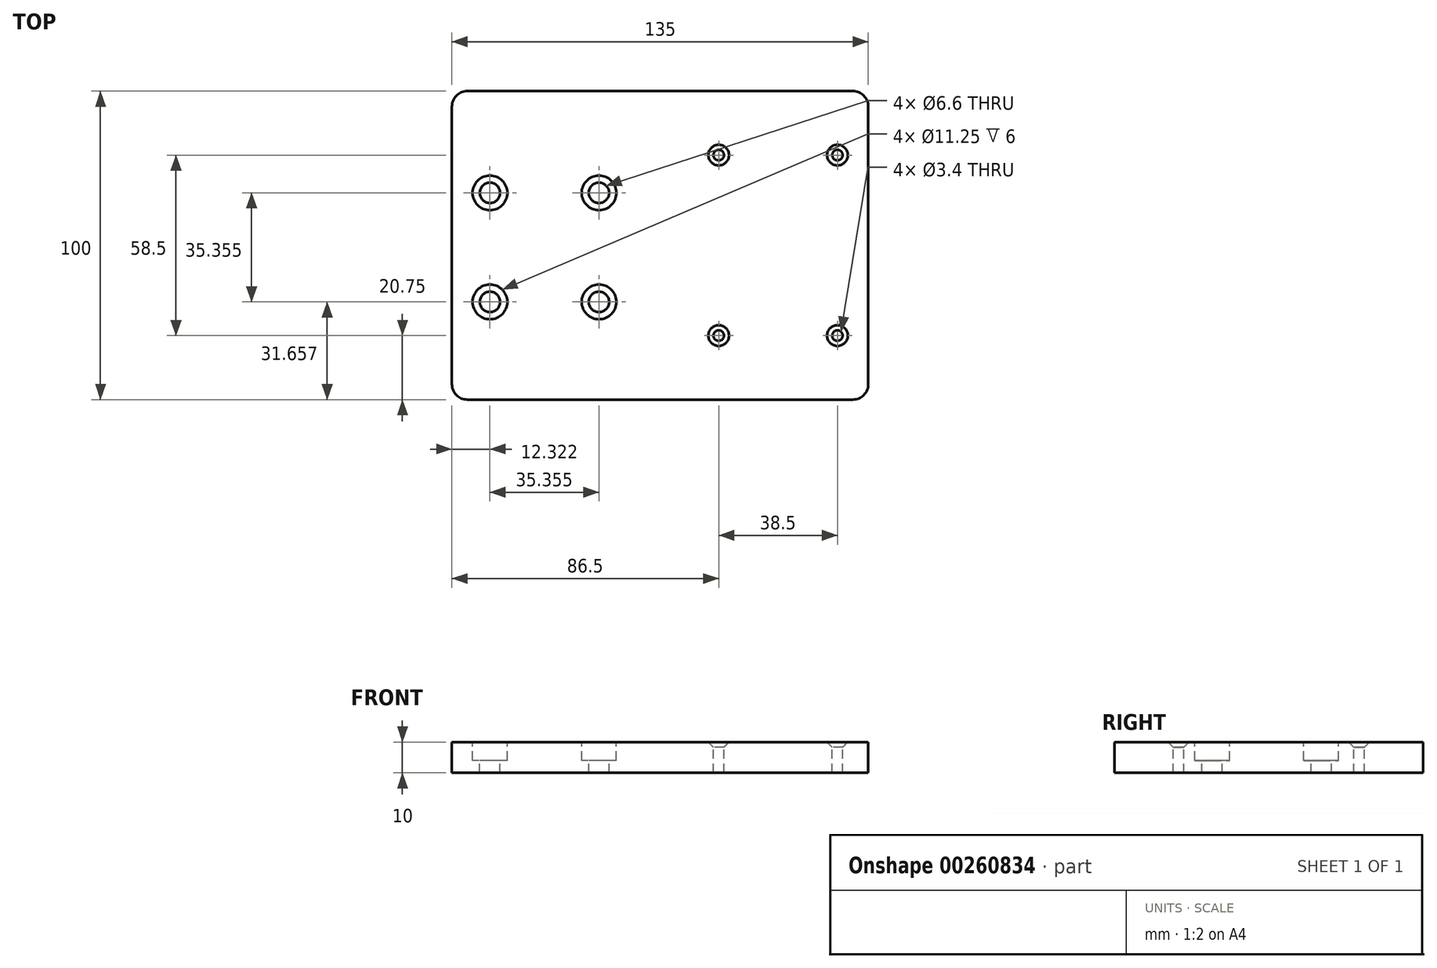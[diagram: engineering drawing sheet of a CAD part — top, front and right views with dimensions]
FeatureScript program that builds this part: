
annotation { "Feature Type Name" : "Feature", "Feature Type Description" : "" }
export const myFeature = defineFeature(function(context is Context, id is Id, definition is map)
    precondition{}
    {
        {
            var Q0;
            Q0=qCreatedBy(makeId("Top.planeOp"),FACE);
            var sketch = newSketch(context, id + "F0", { "sketchPlane" : qUnion([Q0])});
            skLineSegment(sketch, "E0.bottom", {"start": v(0, 0) * mm, "end": v(135, 0) * mm});
            skLineSegment(sketch, "E0.top", {"start": v(0, 100) * mm, "end": v(135, 100) * mm});
            skLineSegment(sketch, "E0.left", {"start": v(0, 0) * mm, "end": v(0, 100) * mm});
            skLineSegment(sketch, "E0.right", {"start": v(135, 0) * mm, "end": v(135, 100) * mm});
            skSolve(sketch);
        }
        {
            var Q0;
            Q0 = qSketchRegion(id + "F0", true);
            extrude(context, id + "F1", {"entities" : qUnion([Q0]), "offsetDistance" : 25 * mm, "depth" : 10 * mm});
        }
        {
            var Q0;
            Q0=makeQuery(id+"F1.opExtrude","CAP_FACE",FACE,{"disambiguationData":[OSD([sQuery(id+"F0.wireOp",EDGE,"E0.bottom"),sQuery(id+"F0.wireOp",EDGE,"E0.top"),sQuery(id+"F0.wireOp",EDGE,"E0.left"),sQuery(id+"F0.wireOp",EDGE,"E0.right")])],"isStart":false});
            var sketch = newSketch(context, id + "F2", { "sketchPlane" : qUnion([Q0])});
            skPoint(sketch, "E1", {"position": v(110, 90) * mm});
            skPoint(sketch, "E2", {"position": v(110, 10) * mm});
            skSolve(sketch);
        }
        {
            var Q0;
            Q0=makeQuery(id+"F1.opExtrude","CAP_FACE",FACE,{"disambiguationData":[OSD([sQuery(id+"F0.wireOp",EDGE,"E0.bottom"),sQuery(id+"F0.wireOp",EDGE,"E0.top"),sQuery(id+"F0.wireOp",EDGE,"E0.left"),sQuery(id+"F0.wireOp",EDGE,"E0.right")])],"isStart":false});
            var sketch = newSketch(context, id + "F3", { "sketchPlane" : qUnion([Q0])});
            skCircle(sketch, "E3", {"center": v(30, 49.33) * mm, "radius": 25 * mm, "construction": true});
            skLineSegment(sketch, "E4", {"start": v(30, 49.33) * mm, "end": v(5, 49.33) * mm, "construction": true});
            skLineSegment(sketch, "E5", {"start": v(30, 49.33) * mm, "end": v(12.32, 67.01) * mm, "construction": true});
            skLineSegment(sketch, "E6", {"start": v(30, 49.33) * mm, "end": v(47.68, 31.66) * mm, "construction": true});
            skLineSegment(sketch, "E7.bottom", {"start": v(12.32, 67.01) * mm, "end": v(47.68, 67.01) * mm, "construction": true});
            skLineSegment(sketch, "E7.top", {"start": v(12.32, 31.66) * mm, "end": v(47.68, 31.66) * mm, "construction": true});
            skLineSegment(sketch, "E7.left", {"start": v(12.32, 67.01) * mm, "end": v(12.32, 31.66) * mm, "construction": true});
            skLineSegment(sketch, "E7.right", {"start": v(47.68, 67.01) * mm, "end": v(47.68, 31.66) * mm, "construction": true});
            skPoint(sketch, "E8", {"position": v(12.32, 67.01) * mm});
            skPoint(sketch, "E9", {"position": v(47.68, 67.01) * mm});
            skPoint(sketch, "E10", {"position": v(47.68, 31.66) * mm});
            skPoint(sketch, "E11", {"position": v(12.32, 31.66) * mm});
            skSolve(sketch);
        }
        {
            var Q0;
            Q0=sQuery(id+"F3.wireOp",VERTEX,"E8");
            var Q1;
            Q1=sQuery(id+"F3.wireOp",VERTEX,"E9");
            var Q2;
            Q2=sQuery(id+"F3.wireOp",VERTEX,"E10");
            var Q3;
            Q3=sQuery(id+"F3.wireOp",VERTEX,"E11");
            var Q4;
            Q4=makeQuery(id+"F1.opExtrude","SWEPT_BODY",BODY,{"disambiguationData":[OSD([sQuery(id+"F0.wireOp",EDGE,"E0.bottom"),sQuery(id+"F0.wireOp",EDGE,"E0.top"),sQuery(id+"F0.wireOp",EDGE,"E0.left"),sQuery(id+"F0.wireOp",EDGE,"E0.right")])]});
            hole(context, id + "F4", {"style" : HoleStyle.C_BORE, "endStyle" : HoleEndStyle.THROUGH, "standardTappedOrClearance" : lookupTablePath({ "fit" : "Normal", "standard" : "ISO", "size" : "M6", "type" : "Clearance" }), "standardBlindInLast" : lookupTablePath({ "fit" : "Normal", "standard" : "ISO", "engagement" : "75%", "pitch" : "1 mm", "size" : "M6", "type" : "Clearance & tapped" }), "holeDiameter" : 6.6 * mm, "cBoreDiameter" : 11.25 * mm, "cBoreDepth" : 6 * mm, "majorDiameter" : 5 * mm, "tappedDepth" : 12 * mm, "tapClearance" : 3, "startFromSketch" : true, "locations" : qUnion([Q0, Q1, Q2, Q3]), "scope" : qUnion([Q4])});
        }
        {
            var Q0;
            Q0=makeQuery(id+"F1.opExtrude","SWEPT_EDGE",EDGE,{"disambiguationData":[OSD([sQuery(id+"F0.wireOp",EDGE,"E0.top"),sQuery(id+"F0.wireOp",EDGE,"E0.left")])]});
            var Q1;
            Q1=makeQuery(id+"F1.opExtrude","SWEPT_EDGE",EDGE,{"disambiguationData":[OSD([sQuery(id+"F0.wireOp",EDGE,"E0.top"),sQuery(id+"F0.wireOp",EDGE,"E0.right")])]});
            var Q2;
            Q2=makeQuery(id+"F1.opExtrude","SWEPT_EDGE",EDGE,{"disambiguationData":[OSD([sQuery(id+"F0.wireOp",EDGE,"E0.bottom"),sQuery(id+"F0.wireOp",EDGE,"E0.right")])]});
            var Q3;
            Q3=makeQuery(id+"F1.opExtrude","SWEPT_EDGE",EDGE,{"disambiguationData":[OSD([sQuery(id+"F0.wireOp",EDGE,"E0.bottom"),sQuery(id+"F0.wireOp",EDGE,"E0.left")])]});
            fillet(context, id + "F5", {"entities" : qUnion([Q0, Q1, Q2, Q3]), "radius" : 5 * mm, "tangentPropagation" : true, "allowEdgeOverflow" : false});
        }
        {
            var Q0;
            Q0=makeQuery(id+"F2.imprint","IMPRINT",FACE,{"disambiguationData":[TD([[makeQuery(id+"F2.imprint","IMPRINT",EDGE,{"derivedFrom":makeQuery(id+"F1.opExtrude","CAP_EDGE",EDGE,{"disambiguationData":[OSD([sQuery(id+"F0.wireOp",EDGE,"E0.bottom")])],"isStart":false})}),1.0]])]});
            var sketch = newSketch(context, id + "F6", { "sketchPlane" : qUnion([Q0])});
            skLineSegment(sketch, "E12.bottom", {"start": v(86.5, 20.75) * mm, "end": v(125, 20.75) * mm});
            skLineSegment(sketch, "E12.top", {"start": v(86.5, 79.25) * mm, "end": v(125, 79.25) * mm});
            skLineSegment(sketch, "E12.left", {"start": v(86.5, 20.75) * mm, "end": v(86.5, 79.25) * mm});
            skLineSegment(sketch, "E12.right", {"start": v(125, 20.75) * mm, "end": v(125, 79.25) * mm});
            skPoint(sketch, "E13", {"position": v(86.5, 20.75) * mm});
            skPoint(sketch, "E14", {"position": v(86.5, 79.25) * mm});
            skPoint(sketch, "E15", {"position": v(125, 79.25) * mm});
            skPoint(sketch, "E16", {"position": v(125, 20.75) * mm});
            skSolve(sketch);
        }
        {
            var Q0;
            Q0=sQuery(id+"F6.wireOp",VERTEX,"E13");
            var Q1;
            Q1=sQuery(id+"F6.wireOp",VERTEX,"E14");
            var Q2;
            Q2=sQuery(id+"F6.wireOp",VERTEX,"E15");
            var Q3;
            Q3=sQuery(id+"F6.wireOp",VERTEX,"E16");
            var Q4;
            Q4=makeQuery(id+"F1.opExtrude","SWEPT_BODY",BODY,{"disambiguationData":[OSD([sQuery(id+"F0.wireOp",EDGE,"E0.bottom"),sQuery(id+"F0.wireOp",EDGE,"E0.top"),sQuery(id+"F0.wireOp",EDGE,"E0.left"),sQuery(id+"F0.wireOp",EDGE,"E0.right")])]});
            hole(context, id + "F7", {"style" : HoleStyle.C_SINK, "endStyle" : HoleEndStyle.THROUGH, "standardTappedOrClearance" : lookupTablePath({ "fit" : "Normal", "standard" : "ISO", "size" : "M3", "type" : "Clearance" }), "standardBlindInLast" : lookupTablePath({ "fit" : "Normal", "standard" : "ISO", "engagement" : "75%", "pitch" : "0.5 mm", "size" : "M3", "type" : "Clearance & tapped" }), "holeDiameter" : 3.4 * mm, "cSinkDiameter" : 6.72 * mm, "cSinkAngle" : 90 * degree, "majorDiameter" : 3 * mm, "isTappedThrough" : true, "tappedDepth" : 12 * mm, "tapClearance" : 3, "startFromSketch" : true, "locations" : qUnion([Q0, Q1, Q2, Q3]), "scope" : qUnion([Q4])});
        }
    });
